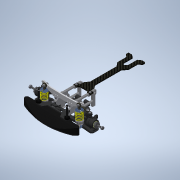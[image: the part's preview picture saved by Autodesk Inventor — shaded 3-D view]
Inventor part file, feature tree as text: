
AUTODESK INVENTOR PART (.ipt)
format: ipt  version: 2020 (Build 240168000, 168)  size: 8,999,424 bytes
history: native  units: mm
features: other x88, sketch x4
ambient origin geometry x8: Origin, YZ Plane, XZ Plane, XY Plane, X Axis, Y Axis, Z Axis, Center Point
bodies: Solid1 (feature_tree)
feature tree (92):
  other  "100-003.iam"
  other  "300-004.iam:1::500-133.ipt:1"
  other  "300-004.iam:1::500-132.ipt:1"
  other  "300-004.iam:1::500-131.ipt:1"
  other  "500-010.ipt:1"
  other  "500-009.ipt:2"
  other  "M3-6.ipt:14"
  other  "M3-6.ipt:15"
  other  "500-171.ipt:1"
  other  "500-172.ipt:1"
  other  "500-169.ipt:1"
  other  "500-172.ipt:2"
  other  "500-171.ipt:2"
  other  "500-169.ipt:2"
  other  "500-124.ipt:1"
  other  "BS 4168 : Part 6  Hexagon Socket Button Head Screw  - Metric M3 x 8:3"
  other  "BS 4168 : Part 6  Hexagon Socket Button Head Screw  - Metric M3 x 8:4"
  other  "M3.ipt:1"
  other  "M3-10.ipt:1"
  other  "M3.ipt:2"
  other  "M3-10.ipt:2"
  other  "500-170.ipt:1"
  other  "300-025.iam:1::300-028.iam:1::21 D - 10 x 14 x 7.ipt:1"
  other  "300-025.iam:1::300-028.iam:1::21 D - 10 x 14 x 7.ipt:2"
  other  "300-025.iam:1::300-028.iam:1::500-140.ipt:1"
  other  "300-025.iam:1::500-126.ipt:2"
  other  "300-025.iam:1::M4.ipt:1"
  other  "300-007.iam:1::500-173.ipt:1"
  other  "300-007.iam:1::500-109.ipt:1"
  other  "300-007.iam:1::BS 4168 : Part 6  Hexagon Socket Button Head Screw  - Metric M3 x 8:1"
  other  "300-007.iam:1::BS 4168 : Part 6  Hexagon Socket Button Head Screw  - Metric M3 x 8:2"
  other  "300-009-04.iam:1::500-000.ipt:1"
  other  "300-009-04.iam:1::500-000.ipt:2"
  other  "300-009-04.iam:1::500-001-02.ipt:1"
  other  "500-109.ipt:1"
  other  "300-010.iam:1::500-106.ipt:1"
  other  "300-010.iam:1::500-100.ipt:1"
  other  "300-010.iam:1::500-102.ipt:1"
  other  "300-010.iam:1::500-104.ipt:1"
  other  "300-010.iam:1::500-109.ipt:1"
  other  "300-010.iam:1::500-109.ipt:2"
  other  "300-010.iam:1::500-107.ipt:1"
  other  "300-010.iam:1::500-105.ipt:1"
  other  "300-010.iam:1::500-103.ipt:2"
  other  "300-010.iam:1::Compression Spring 16:1"
  other  "500-175.ipt:1"
  other  "300-027.iam:1::300-020.iam:1::21 D - 10 x 14 x 7.ipt:1"
  other  "300-027.iam:1::300-020.iam:1::21 D - 10 x 14 x 7.ipt:2"
  other  "300-027.iam:1::300-020.iam:1::500-134.ipt:1"
  other  "300-027.iam:1::500-129.ipt:2"
  other  "300-027.iam:1::M4.ipt:1"
  other  "300-007.iam:2::500-173.ipt:1"
  other  "300-007.iam:2::500-109.ipt:1"
  other  "300-007.iam:2::BS 4168 : Part 6  Hexagon Socket Button Head Screw  - Metric M3 x 8:1"
  other  "300-007.iam:2::BS 4168 : Part 6  Hexagon Socket Button Head Screw  - Metric M3 x 8:2"
  other  "300-010.iam:2::500-106.ipt:1"
  other  "300-010.iam:2::500-100.ipt:1"
  other  "300-010.iam:2::500-102.ipt:1"
  other  "300-010.iam:2::500-104.ipt:1"
  other  "300-010.iam:2::500-109.ipt:1"
  other  "300-010.iam:2::500-109.ipt:2"
  other  "300-010.iam:2::500-107.ipt:1"
  other  "300-010.iam:2::500-105.ipt:1"
  other  "300-010.iam:2::500-103.ipt:2"
  other  "300-010.iam:2::Compression Spring 16:1"
  other  "300-009-04.iam:2::500-000.ipt:1"
  other  "300-009-04.iam:2::500-000.ipt:2"
  other  "300-009-04.iam:2::500-001-02.ipt:1"
  other  "500-109.ipt:2"
  other  "500-010.ipt:2"
  other  "300-032.iam:1::500-180.ipt:1"
  other  "300-032.iam:1::500-179.ipt:1"
  other  "300-032.iam:1::500-177.ipt:1"
  other  "300-032.iam:2::500-180.ipt:1"
  other  "300-032.iam:2::500-179.ipt:1"
  other  "300-032.iam:2::500-177.ipt:1"
  other  "BS 4168 : Part 6  Hexagon Socket Button Head Screw  - Metric M3 x 8:5"
  other  "BS 4168 : Part 6  Hexagon Socket Button Head Screw  - Metric M3 x 8:6"
  other  "M3-10.ipt:3"
  other  "M3-10.ipt:4"
  other  "Work Point1"
  other  "Work Point1_1"
  other  "Work Point1_2"
  sketch  "Sketch9"
  sketch  "Sketch9_1"  dims[d0=10.0mm]
  other  "Work Point1_3"
  other  "Work Point1_4"
  sketch  "Sketch9_2"  dims[d31=0.5mm]
  sketch  "Sketch9_3"
  other  "Work Point1_5"
  other  "Work Point1_6"
  other  "Work Point1_7"
